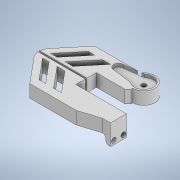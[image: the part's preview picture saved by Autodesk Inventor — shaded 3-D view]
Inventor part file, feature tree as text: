
AUTODESK INVENTOR PART (.ipt)
format: ipt  version: 2021 (Build 250183000, 183)  size: 258,560 bytes
history: native  units: mm
features: extrude x10, sketch x10, other x1, fillet x1, chamfer x1
ambient origin geometry x8: Origin, YZ Plane, XZ Plane, XY Plane, X Axis, Y Axis, Z Axis, Center Point
bodies: Body1 (feature_tree)
feature tree (23):
  other  "Sólido1"
  extrude  "Extrusión1"  Depth=6.0mm
  extrude  "Extrusión2"  Depth=8.0mm TaperAngle=0.0deg
  extrude  "Extrusión3"  Depth=6.0mm TaperAngle=0.0deg
  extrude  "Extrusión4"  Depth=8.0mm TaperAngle=0.0deg
  extrude  "Extrusión5"  Depth=2.0mm
  extrude  "Extrusión6"  Depth=3.0mm
  extrude  "Extrusión7"  Depth=3.0mm TaperAngle=0.0deg
  extrude  "Extrusión8"  Depth=3.0mm TaperAngle=0.0deg
  fillet  "Empalme1"  Radius=5.0mm
  chamfer  "Chaflán1"  Distance=5.0mm
  extrude  "Extrusión9"  Depth=2.0mm
  extrude  "Extrusión10"  Depth=2.0mm
  sketch  "Boceto1"  dims[d1=6.0mm d8=6.0mm]
  sketch  "Boceto2"  dims[d9=0.5mm d10=8.0mm d11=0.0mm]
  sketch  "Boceto3"  dims[d12=6.0mm d13=4.0mm d14=0.0mm]
  sketch  "Boceto4"  dims[d15=5.0mm d16=8.0mm d17=0.0mm]
  sketch  "Boceto5"  dims[d18=5.0mm d19=2.0mm]
  sketch  "Boceto6"  dims[d20=2.0mm d21=3.0mm]
  sketch  "Boceto7"  dims[d22=3.0mm d23=3.0mm d24=0.0mm]
  sketch  "Boceto8"  dims[d25=3.0mm d26=5.0mm d27=0.0mm d28=5.0mm]
  sketch  "Boceto9"  dims[d29=5.0mm]
  sketch  "Boceto10"  dims[d30=5.0mm d31=5.0mm d32=5.0mm d33=5.0mm d34=5.0mm d35=5.0mm d36=5.0mm d37=10.0mm d38=0.0mm d39=10.0mm d40=0.0mm d41=8.0mm d42=0.0mm d43=2.0mm d44=2.0mm d45=2.0mm d46=45.0deg d47=6.0mm d48=4.0mm d49=0.0mm d50=12.0mm d51=19.0mm d52=4.5mm d53=9.0mm d54=3.0mm d55=2.0mm d56=0.0mm]
